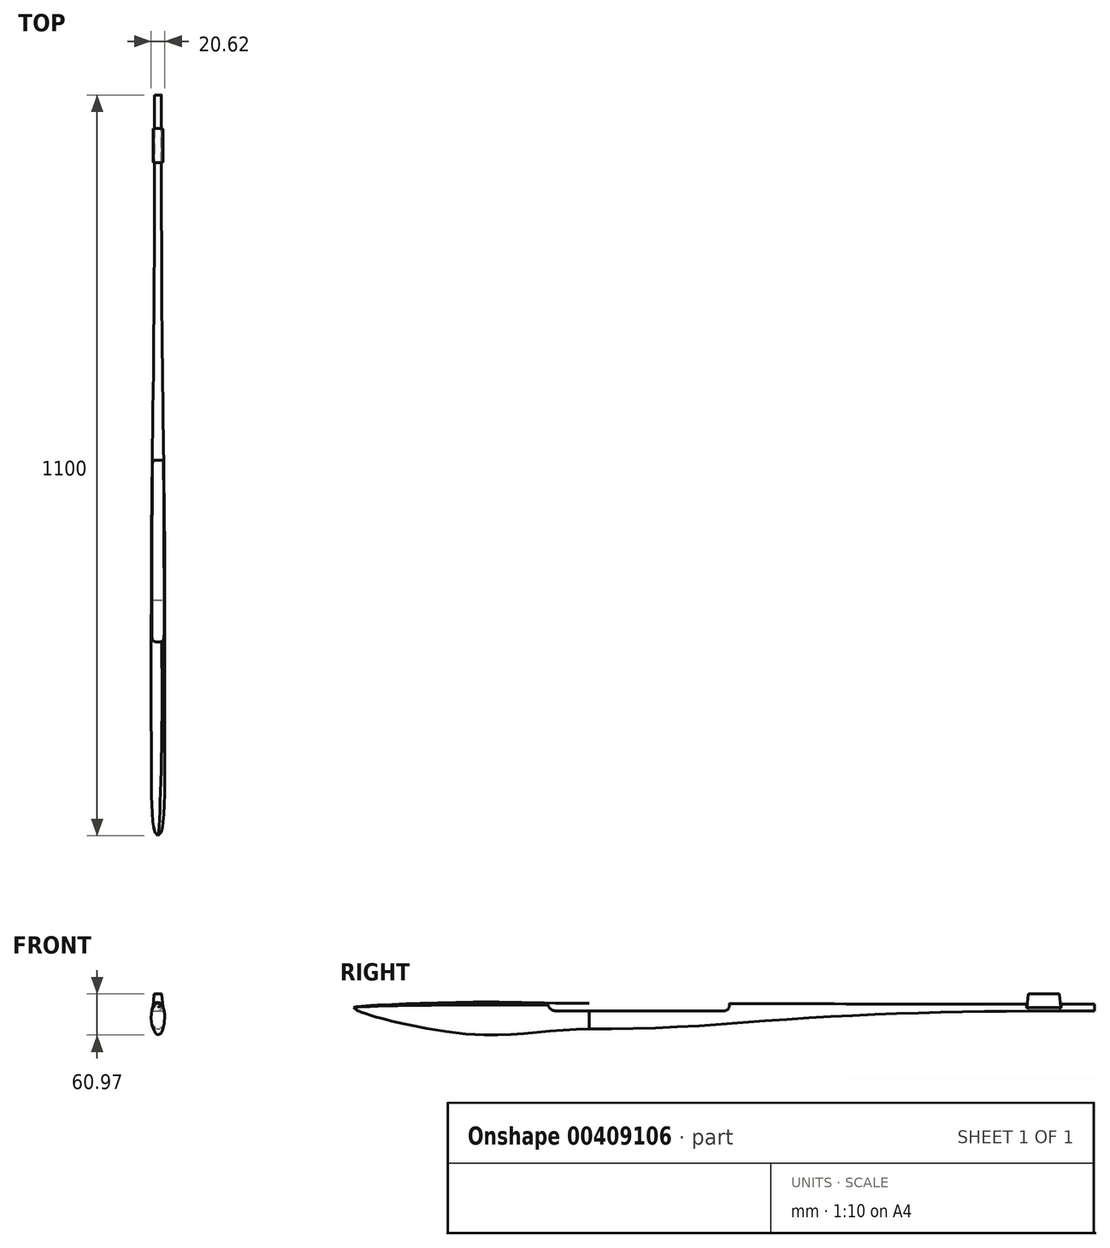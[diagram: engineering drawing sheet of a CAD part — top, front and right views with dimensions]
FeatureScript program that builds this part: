
annotation { "Feature Type Name" : "Feature", "Feature Type Description" : "" }
export const myFeature = defineFeature(function(context is Context, id is Id, definition is map)
    precondition{}
    {
        {
            var Q0;
            Q0=qCreatedBy(makeId("Front.planeOp"),FACE);
            var sketch = newSketch(context, id + "F0", { "sketchPlane" : qUnion([Q0])});
            skEllipse(sketch, "E0", {"center": v(0, 0) * mm, "majorRadius": 22.5 * mm, "minorRadius": 10 * mm, "majorAxis": v(0, 1)});
            skPoint(sketch, "E1", {"position": v(0, 22.5) * mm});
            skPoint(sketch, "E2", {"position": v(0, -22.5) * mm});
            skPoint(sketch, "E3", {"position": v(10, 0) * mm});
            skPoint(sketch, "E4", {"position": v(-10, 0) * mm});
            skLineSegment(sketch, "E5", {"start": v(-10, 0) * mm, "end": v(10, 0) * mm, "construction": true});
            skLineSegment(sketch, "E6", {"start": v(0, 22.5) * mm, "end": v(0, -22.5) * mm, "construction": true});
            skSolve(sketch);
        }
        {
            var Q0;
            Q0=qCreatedBy(makeId("Front.planeOp"),FACE);
            cPlane(context, id + "F1", {"entities" : qUnion([Q0]), "cplaneType" : CPlaneType.OFFSET, "offset" : 150 * mm, "width" : 150 * mm, "height" : 150 * mm});
        }
        {
            var Q0;
            Q0=qCreatedBy(id+"F1.planeOp",FACE);
            var sketch = newSketch(context, id + "F2", { "sketchPlane" : qUnion([Q0])});
            skPoint(sketch, "E7.0", {"position": v(0, 15) * mm});
            skLineSegment(sketch, "E8", {"start": v(0, 15) * mm, "end": v(0, 0) * mm, "construction": true});
            skSolve(sketch);
        }
        {
            var Q0;
            Q0=qCreatedBy(id+"F1.planeOp",FACE);
            cPlane(context, id + "F3", {"entities" : qUnion([Q0]), "cplaneType" : CPlaneType.OFFSET, "offset" : 350 * mm, "oppositeDirection" : true, "width" : 150 * mm, "height" : 150 * mm});
        }
        {
            var Q0;
            Q0=qCreatedBy(id+"F1.planeOp",FACE);
            cPlane(context, id + "F4", {"entities" : qUnion([Q0]), "cplaneType" : CPlaneType.OFFSET, "offset" : 1100 * mm, "oppositeDirection" : true, "width" : 150 * mm, "height" : 150 * mm});
        }
        {
            var Q0;
            Q0=qCreatedBy(id+"F3.planeOp",FACE);
            var sketch = newSketch(context, id + "F5", { "sketchPlane" : qUnion([Q0])});
            skEllipse(sketch, "E9", {"center": v(0, 2) * mm, "majorRadius": 19 * mm, "minorRadius": 10 * mm, "majorAxis": v(0, 1)});
            skLineSegment(sketch, "E10", {"start": v(0, 2) * mm, "end": v(0, 0) * mm, "construction": true});
            skSolve(sketch);
        }
        {
            var Q0;
            Q0=qCreatedBy(id+"F4.planeOp",FACE);
            var sketch = newSketch(context, id + "F6", { "sketchPlane" : qUnion([Q0])});
            skCircle(sketch, "E11", {"center": v(0, 15) * mm, "radius": 5 * mm});
            skLineSegment(sketch, "E12", {"start": v(0, 15) * mm, "end": v(0, 0) * mm, "construction": true});
            skSolve(sketch);
        }
        {
            var Q0;
            Q0=sQuery(id+"F2.wireOp",VERTEX,"E7.0");
            var Q1;
            Q1=makeQuery(id+"F0.imprint","IMPRINT",FACE,{"disambiguationData":[TD([[makeQuery(id+"F0.imprint","IMPRINT",EDGE,{"derivedFrom":sQuery(id+"F0.wireOp",EDGE,"E0")}),1.0]])]});
            var Q2;
            Q2=makeQuery(id+"F5.imprint","IMPRINT",FACE,{"disambiguationData":[TD([[makeQuery(id+"F5.imprint","IMPRINT",EDGE,{"derivedFrom":sQuery(id+"F5.wireOp",EDGE,"E9")}),1.0]])]});
            loft(context, id + "F7", {"startCondition" : LoftEndDerivativeType.TANGENT_TO_PROFILE, "startMagnitude" : 1, "endCondition" : LoftEndDerivativeType.NORMAL_TO_PROFILE, "endMagnitude" : 1, "sheetProfilesArray" : [{ "sheetProfileEntities" : qUnion([Q0]) }, { "sheetProfileEntities" : qUnion([Q1]) }, { "sheetProfileEntities" : qUnion([Q2]) }]});
        }
        {
            var Q0;
            Q0 = qSketchRegion(id + "F5", true);
            var Q1;
            Q1 = qSketchRegion(id + "F6", true);
            var Q2;
            Q2=sQuery(id+"FIQjEDsbj7QhTGf_1.wireOp",EDGE,"6759e5f3-4bc8-4458-9988-c7c3a2fc2b3b");
            loft(context, id + "F8", {"operationType" : NewBodyOperationType.ADD, "startCondition" : LoftEndDerivativeType.NORMAL_TO_PROFILE, "startMagnitude" : 1, "endCondition" : LoftEndDerivativeType.NORMAL_TO_PROFILE, "endMagnitude" : 2, "sheetProfilesArray" : [{ "sheetProfileEntities" : qUnion([Q0]) }, { "sheetProfileEntities" : qUnion([Q1]) }], "guidesArray" : [{ "guideEntities" : qUnion([Q2]), "guideDerivativeType" : LoftGuideDerivativeType.DEFAULT, "guideDerivativeMagnitude" : 1 }]});
        }
        {
            var Q0;
            Q0=qCreatedBy(makeId("Right.planeOp"),FACE);
            var sketch = newSketch(context, id + "F9", { "sketchPlane" : qUnion([Q0])});
            skLineSegment(sketch, "E13", {"start": v(150, 10) * mm, "end": v(400, 10) * mm});
            skArc(sketch, "E14", {"start": v(400, 10) * mm, "mid": v(408, 18) * mm, "end": v(400, 26) * mm});
            skLineSegment(sketch, "E15", {"start": v(400, 26) * mm, "end": v(150.38, 34) * mm});
            skArc(sketch, "E16", {"start": v(150.38, 34) * mm, "mid": v(138, 22.2) * mm, "end": v(150, 10) * mm});
            skSolve(sketch);
        }
        {
            var Q0;
            Q0 = qSketchRegion(id + "F9", true);
            extrude(context, id + "F10", {"entities" : qUnion([Q0]), "operationType" : NewBodyOperationType.REMOVE, "endBound" : BoundingType.THROUGH_ALL, "oppositeDirection" : true, "depth" : 25 * mm, "hasSecondDirection" : true, "secondDirectionBound" : SecondDirectionBoundingType.THROUGH_ALL, "secondDirectionOppositeDirection" : false, "secondDirectionDepth" : 25 * mm});
        }
        {
            var Q0;
            Q0=qCreatedBy(makeId("Top.planeOp"),FACE);
            var Q1;
            Q1=sQuery(id+"F6.wireOp",VERTEX,"E11.center");
            cPlane(context, id + "F11", {"entities" : qUnion([Q0, Q1]), "cplaneType" : CPlaneType.PLANE_POINT, "offset" : 25 * mm, "width" : 150 * mm, "height" : 150 * mm});
        }
        {
            var Q0;
            Q0=qCreatedBy(id+"F11.planeOp",FACE);
            var sketch = newSketch(context, id + "F12", { "sketchPlane" : qUnion([Q0])});
            skLineSegment(sketch, "E17.bottom", {"start": v(-7.5, 900) * mm, "end": v(7.5, 900) * mm});
            skLineSegment(sketch, "E17.top", {"start": v(-7.5, 850) * mm, "end": v(7.5, 850) * mm});
            skLineSegment(sketch, "E17.left", {"start": v(-7.5, 900) * mm, "end": v(-7.5, 850) * mm});
            skLineSegment(sketch, "E17.right", {"start": v(7.5, 900) * mm, "end": v(7.5, 850) * mm});
            skPoint(sketch, "E18", {"position": v(0, 900) * mm});
            skSolve(sketch);
        }
        {
            var Q0;
            Q0 = qSketchRegion(id + "F12", true);
            extrude(context, id + "F13", {"entities" : qUnion([Q0]), "operationType" : NewBodyOperationType.ADD, "depth" : 20 * mm, "hasDraft" : true, "draftAngle" : 5 * degree, "draftPullDirection" : true});
        }
        {
            var Q0;
            Q0=makeQuery(id+"F13.opExtrude","SWEPT_FACE",FACE,{"disambiguationData":[OSD([sQuery(id+"F12.wireOp",EDGE,"E17.bottom")])]});
            var Q1;
            Q1=makeQuery(id+"F13.opExtrude","SWEPT_FACE",FACE,{"disambiguationData":[OSD([sQuery(id+"F12.wireOp",EDGE,"E17.top")])]});
            var Q2;
            Q2=makeQuery(id+"F13.opExtrude","SWEPT_FACE",FACE,{"disambiguationData":[OSD([sQuery(id+"F12.wireOp",EDGE,"E17.right")])]});
            var Q3;
            Q3=makeQuery(id+"F13.opExtrude","SWEPT_FACE",FACE,{"disambiguationData":[OSD([sQuery(id+"F12.wireOp",EDGE,"E17.left")])]});
            fillet(context, id + "F14", {"entities" : qUnion([Q0, Q1, Q2, Q3]), "radius" : 1 * mm, "tangentPropagation" : true, "allowEdgeOverflow" : false});
        }
    });
